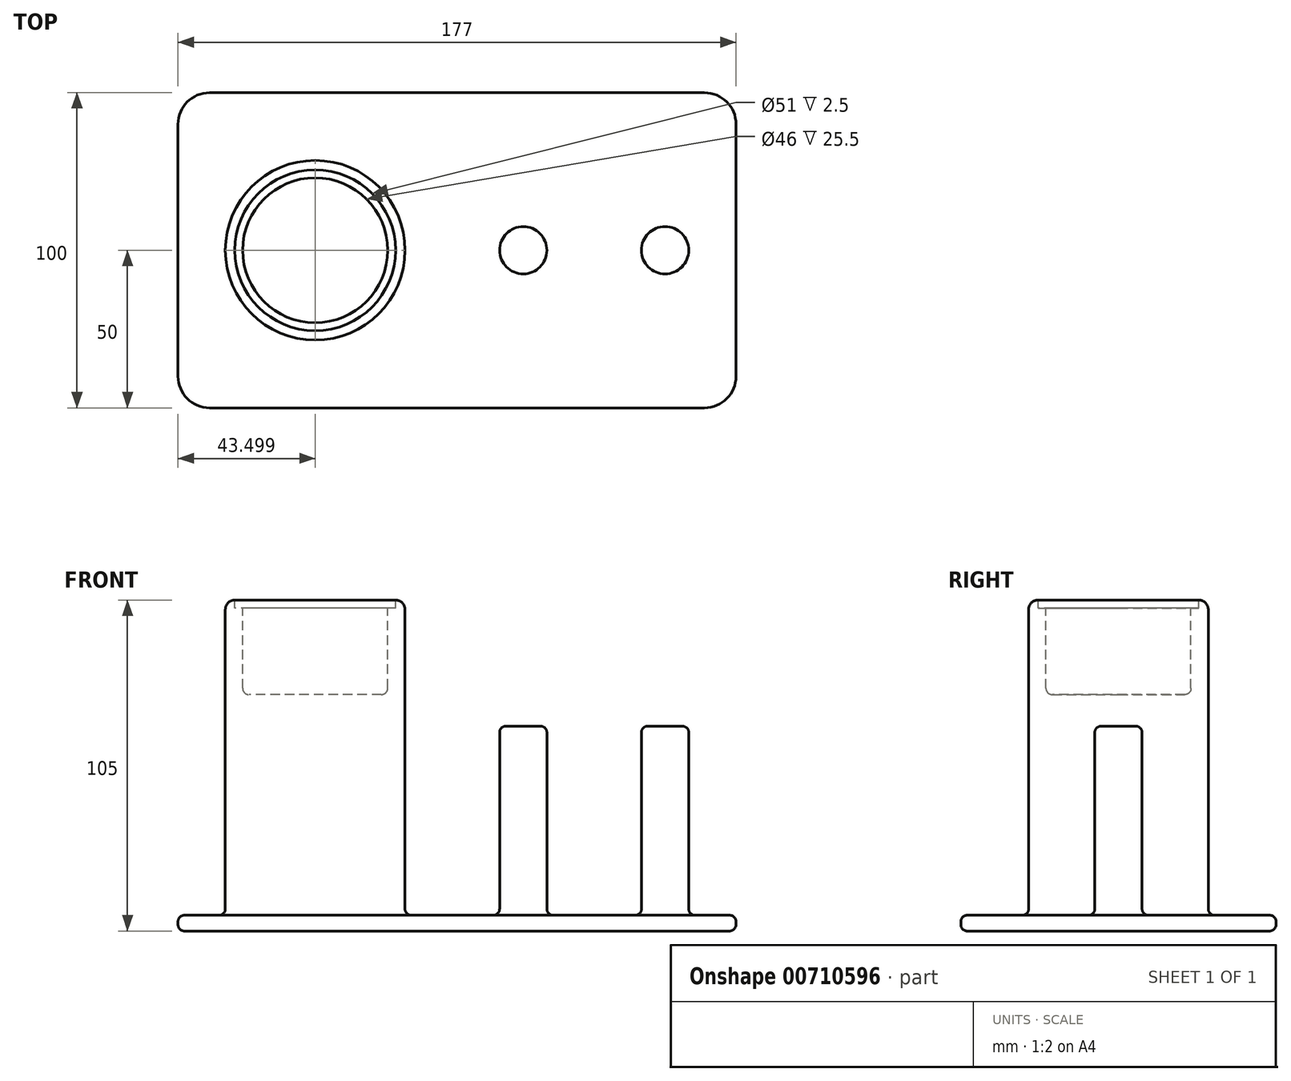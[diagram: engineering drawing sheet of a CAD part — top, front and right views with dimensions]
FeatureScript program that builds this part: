
annotation { "Feature Type Name" : "Feature", "Feature Type Description" : "" }
export const myFeature = defineFeature(function(context is Context, id is Id, definition is map)
    precondition{}
    {
        {
            var Q0;
            Q0=qCreatedBy(makeId("Top.planeOp"),FACE);
            var sketch = newSketch(context, id + "F0", { "sketchPlane" : qUnion([Q0])});
            skLineSegment(sketch, "E0", {"start": v(-122.74, 100) * mm, "end": v(-122.74, 0) * mm});
            skLineSegment(sketch, "E1", {"start": v(-122.74, 0) * mm, "end": v(54.26, 0) * mm});
            skLineSegment(sketch, "E2", {"start": v(54.26, 0) * mm, "end": v(54.26, 100) * mm});
            skLineSegment(sketch, "E3", {"start": v(-122.74, 100) * mm, "end": v(54.26, 100) * mm});
            skSolve(sketch);
        }
        {
            var Q0;
            Q0 = qSketchRegion(id + "F0", true);
            extrude(context, id + "F1", {"entities" : qUnion([Q0]), "depth" : 5 * mm, "offsetDistance" : 25 * mm});
        }
        {
            var Q0;
            Q0=makeQuery(id+"F1.opExtrude","CAP_FACE",FACE,{"disambiguationData":[OSD([sQuery(id+"F0.wireOp",EDGE,"E0"),sQuery(id+"F0.wireOp",EDGE,"E1"),sQuery(id+"F0.wireOp",EDGE,"E2"),sQuery(id+"F0.wireOp",EDGE,"E3")])],"isStart":false});
            var sketch = newSketch(context, id + "F2", { "sketchPlane" : qUnion([Q0])});
            skCircle(sketch, "E4", {"center": v(-79.24, 50) * mm, "radius": 28.5 * mm});
            skCircle(sketch, "E5", {"center": v(-13.24, 50) * mm, "radius": 7.5 * mm});
            skLineSegment(sketch, "E6", {"start": v(-79.24, 50) * mm, "end": v(103.4, 50) * mm, "construction": true});
            skCircle(sketch, "E7", {"center": v(31.76, 50) * mm, "radius": 7.5 * mm});
            skSolve(sketch);
        }
        {
            var Q0;
            Q0=makeQuery(id+"F2.imprint","IMPRINT",FACE,{"disambiguationData":[TD([[makeQuery(id+"F2.imprint","IMPRINT",EDGE,{"derivedFrom":sQuery(id+"F2.wireOp",EDGE,"E4")}),1.0]])]});
            extrude(context, id + "F3", {"entities" : qUnion([Q0]), "operationType" : NewBodyOperationType.ADD, "depth" : 100 * mm, "offsetDistance" : 25 * mm});
        }
        {
            var Q0;
            Q0=makeQuery(id+"F1.opExtrude","SWEPT_EDGE",EDGE,{"disambiguationData":[OSD([sQuery(id+"F0.wireOp",EDGE,"E0"),sQuery(id+"F0.wireOp",EDGE,"E1")])]});
            var Q1;
            Q1=makeQuery(id+"F1.opExtrude","SWEPT_EDGE",EDGE,{"disambiguationData":[OSD([sQuery(id+"F0.wireOp",EDGE,"E1"),sQuery(id+"F0.wireOp",EDGE,"E2")])]});
            var Q2;
            Q2=makeQuery(id+"F1.opExtrude","SWEPT_EDGE",EDGE,{"disambiguationData":[OSD([sQuery(id+"F0.wireOp",EDGE,"E0"),sQuery(id+"F0.wireOp",EDGE,"E3")])]});
            var Q3;
            Q3=makeQuery(id+"F1.opExtrude","SWEPT_EDGE",EDGE,{"disambiguationData":[OSD([sQuery(id+"F0.wireOp",EDGE,"E2"),sQuery(id+"F0.wireOp",EDGE,"E3")])]});
            fillet(context, id + "F4", {"entities" : qUnion([Q0, Q1, Q2, Q3]), "radius" : 10 * mm, "tangentPropagation" : true, "allowEdgeOverflow" : false});
        }
        {
            var Q0;
            Q0=makeQuery(id+"Fn1qHCrQsfIdUsP_1.opExtrude","CAP_EDGE",EDGE,{"disambiguationData":[OSD([sQuery(id+"FqaJWfYasBYhKSK_1.wireOp",EDGE,"v4obqR0k-AeLG-3NqG-HtXY-6FBkIrhS5mJg")])],"isStart":false});
            var Q1;
            Q1=makeQuery(id+"F3.opExtrude","CAP_EDGE",EDGE,{"disambiguationData":[OSD([sQuery(id+"F2.wireOp",EDGE,"E4")])],"isStart":false});
            fillet(context, id + "F5", {"entities" : qUnion([Q0, Q1]), "radius" : 3 * mm, "tangentPropagation" : true, "allowEdgeOverflow" : false});
        }
        {
            var Q0;
            Q0=makeQuery(id+"F3.opExtrude","CAP_FACE",FACE,{"disambiguationData":[OSD([sQuery(id+"F2.wireOp",EDGE,"E4")])],"isStart":false});
            var Q1;
            Q1=makeQuery(id+"Fn1qHCrQsfIdUsP_1.opExtrude","CAP_FACE",FACE,{"disambiguationData":[OSD([sQuery(id+"FqaJWfYasBYhKSK_1.wireOp",EDGE,"v4obqR0k-AeLG-3NqG-HtXY-6FBkIrhS5mJg")])],"isStart":false});
            extrude(context, id + "F6", {"entities" : qUnion([Q0, Q1]), "operationType" : NewBodyOperationType.REMOVE, "oppositeDirection" : true, "depth" : 2.5 * mm, "offsetDistance" : 25 * mm});
        }
        {
            var Q0;
            Q0=makeQuery(id+"F6.boolean.opBoolean","COPY",FACE,{"derivedFrom":makeQuery(id+"F6.opExtrude","CAP_FACE",FACE,{"disambiguationData":[OSD([sQuery(id+"F2.wireOp",EDGE,"E4")])],"isStart":false})});
            var sketch = newSketch(context, id + "F7", { "sketchPlane" : qUnion([Q0])});
            skCircle(sketch, "E8.0", {"center": v(-79.24, 50) * mm, "radius": 23 * mm});
            skSolve(sketch);
        }
        {
            var Q0;
            Q0 = qSketchRegion(id + "F7", true);
            extrude(context, id + "F8", {"entities" : qUnion([Q0]), "operationType" : NewBodyOperationType.REMOVE, "oppositeDirection" : true, "depth" : 27.5 * mm, "offsetDistance" : 25 * mm});
        }
        {
            var Q0;
            Q0=makeQuery(id+"F2.imprint","IMPRINT",FACE,{"disambiguationData":[TD([[makeQuery(id+"F2.imprint","IMPRINT",EDGE,{"derivedFrom":sQuery(id+"F2.wireOp",EDGE,"E7")}),1.0]])]});
            var Q1;
            Q1=makeQuery(id+"F2.imprint","IMPRINT",FACE,{"disambiguationData":[TD([[makeQuery(id+"F2.imprint","IMPRINT",EDGE,{"derivedFrom":sQuery(id+"F2.wireOp",EDGE,"E5")}),1.0]])]});
            var Q2;
            Q2=sQuery(id+"F2.wireOp",EDGE,"E7");
            var Q3;
            Q3=sQuery(id+"F2.wireOp",EDGE,"E5");
            extrude(context, id + "F9", {"entities" : qUnion([Q0, Q1]), "operationType" : NewBodyOperationType.ADD, "surfaceEntities" : qUnion([Q2, Q3]), "depth" : 60 * mm, "offsetDistance" : 25 * mm});
        }
        {
            var Q0;
            Q0=makeQuery(id+"F1.opExtrude","CAP_FACE",FACE,{"disambiguationData":[OSD([sQuery(id+"F0.wireOp",EDGE,"E0"),sQuery(id+"F0.wireOp",EDGE,"E1"),sQuery(id+"F0.wireOp",EDGE,"E2"),sQuery(id+"F0.wireOp",EDGE,"E3")])],"isStart":false});
            var Q1;
            Q1=makeQuery(id+"F1.opExtrude","CAP_FACE",FACE,{"disambiguationData":[OSD([sQuery(id+"F0.wireOp",EDGE,"E0"),sQuery(id+"F0.wireOp",EDGE,"E1"),sQuery(id+"F0.wireOp",EDGE,"E2"),sQuery(id+"F0.wireOp",EDGE,"E3")])],"isStart":true});
            var Q2;
            Q2=makeQuery(id+"F8.boolean.opBoolean","COPY",EDGE,{"derivedFrom":makeQuery(id+"F8.opExtrude","CAP_EDGE",EDGE,{"disambiguationData":[OSD([sQuery(id+"F7.wireOp",EDGE,"E8.0")])],"isStart":false})});
            var Q3;
            Q3=makeQuery(id+"F9.opExtrude","CAP_EDGE",EDGE,{"disambiguationData":[OSD([sQuery(id+"F2.wireOp",EDGE,"E7")])],"isStart":false});
            var Q4;
            Q4=makeQuery(id+"F9.opExtrude","CAP_EDGE",EDGE,{"disambiguationData":[OSD([sQuery(id+"F2.wireOp",EDGE,"E5")])],"isStart":false});
            fillet(context, id + "F10", {"entities" : qUnion([Q0, Q1, Q2, Q3, Q4]), "radius" : 2 * mm, "tangentPropagation" : true, "allowEdgeOverflow" : false});
        }
    });
